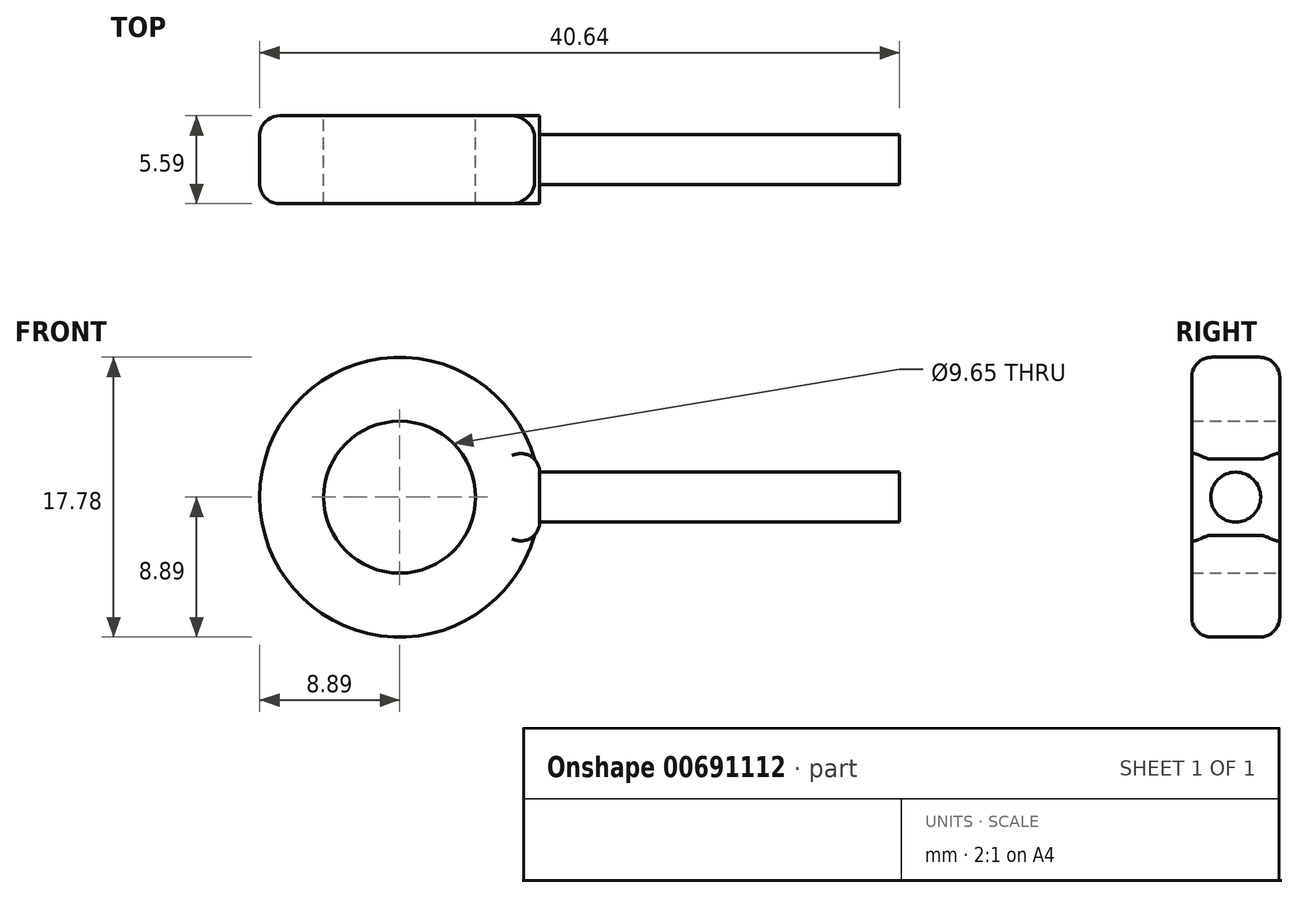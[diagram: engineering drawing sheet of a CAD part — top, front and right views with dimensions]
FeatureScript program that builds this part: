
annotation { "Feature Type Name" : "Feature", "Feature Type Description" : "" }
export const myFeature = defineFeature(function(context is Context, id is Id, definition is map)
    precondition{}
    {
        {
            var Q0;
            Q0=qCreatedBy(makeId("Front.planeOp"),FACE);
            var sketch = newSketch(context, id + "F0", { "sketchPlane" : qUnion([Q0])});
            skLineSegment(sketch, "E0", {"start": v(0, 0) * mm, "end": v(-95.2, 0) * mm, "construction": true});
            skLineSegment(sketch, "E1", {"start": v(0, 0) * mm, "end": v(0, 1.59) * mm});
            skLineSegment(sketch, "E2", {"start": v(0, 1.59) * mm, "end": v(-22.86, 1.59) * mm});
            skLineSegment(sketch, "E3.MirrorCS", {"start": v(0, -1.59) * mm, "end": v(-22.86, -1.59) * mm});
            skLineSegment(sketch, "E4.MirrorCS", {"start": v(0, 0) * mm, "end": v(0, -1.59) * mm});
            skLineSegment(sketch, "E5", {"start": v(-22.86, 1.59) * mm, "end": v(-22.86, -1.59) * mm});
            skArc(sketch, "E6", {"start": v(-23.2, 2.41) * mm, "mid": v(-40.64, 0) * mm, "end": v(-23.2, -2.41) * mm});
            skArc(sketch, "E7", {"start": v(-22.86, 1.59) * mm, "mid": v(-22.95, 2.03) * mm, "end": v(-23.2, 2.41) * mm});
            skArc(sketch, "E8", {"start": v(-22.86, -1.59) * mm, "mid": v(-22.95, -2.03) * mm, "end": v(-23.2, -2.41) * mm});
            skLineSegment(sketch, "E9", {"start": v(-23.2, 2.41) * mm, "end": v(-23.2, 0) * mm, "construction": true});
            skLineSegment(sketch, "E10", {"start": v(-23.2, 0) * mm, "end": v(-23.2, -2.41) * mm, "construction": true});
            skCircle(sketch, "E11", {"center": v(-31.75, 0) * mm, "radius": 4.83 * mm});
            skSolve(sketch);
        }
        {
            var Q0;
            Q0=makeQuery(id+"F0.imprint","IMPRINT",FACE,{"disambiguationData":[TD([[makeQuery(id+"F0.imprint","IMPRINT",EDGE,{"derivedFrom":sQuery(id+"F0.wireOp",EDGE,"E5")}),-1.0]])]});
            var Q1;
            Q1=makeQuery(id+"F0.imprint","IMPRINT",FACE,{"disambiguationData":[TD([[makeQuery(id+"F0.imprint","IMPRINT",EDGE,{"derivedFrom":sQuery(id+"F0.wireOp",EDGE,"E1")}),1.0]])]});
            extrude(context, id + "F1", {"entities" : qUnion([Q0, Q1]), "depth" : 5.6 * mm, "offsetDistance" : 25.4 * mm});
        }
        {
            var Q0;
            Q0=makeQuery(id+"F1.opExtrude","SWEPT_FACE",FACE,{"disambiguationData":[OSD([sQuery(id+"F0.wireOp",EDGE,"E1"),sQuery(id+"F0.wireOp",EDGE,"E4.MirrorCS")])]});
            var sketch = newSketch(context, id + "F2", { "sketchPlane" : qUnion([Q0])});
            skCircle(sketch, "E12", {"center": v(-2.8, 0) * mm, "radius": 1.59 * mm});
            skLineSegment(sketch, "E13", {"start": v(-5.59, -1.59) * mm, "end": v(-5.59, 1.59) * mm});
            skLineSegment(sketch, "E14", {"start": v(-5.59, 1.59) * mm, "end": v(0, 1.59) * mm});
            skLineSegment(sketch, "E15", {"start": v(0, 1.59) * mm, "end": v(0, -1.59) * mm});
            skLineSegment(sketch, "E16", {"start": v(0, -1.59) * mm, "end": v(-5.59, -1.59) * mm});
            skLineSegment(sketch, "E17", {"start": v(-5.59, 1.59) * mm, "end": v(0, -1.59) * mm, "construction": true});
            skSolve(sketch);
        }
        {
            var Q0;
            {var subQ0=sQuery(id+"F2.wireOp",EDGE,"E13");var subQ1=sQuery(id+"F2.wireOp",EDGE,"E12");var subQ2=makeQuery(id+"F2.imprint","INTERSECT",VERTEX,{"derivedFrom":[subQ1,subQ0]});Q0=makeQuery(id+"F2.imprint","IMPRINT",FACE,{"disambiguationData":[TD([[makeQuery(id+"F2.imprint","IMPRINT",EDGE,{"disambiguationData":[TD([[subQ2,-1.0]])],"derivedFrom":subQ1}),-1.0]])]});}
            var Q1;
            {var subQ0=sQuery(id+"F2.wireOp",EDGE,"E14");var subQ1=sQuery(id+"F2.wireOp",EDGE,"E12");var subQ2=makeQuery(id+"F2.imprint","INTERSECT",VERTEX,{"derivedFrom":[subQ1,subQ0]});Q1=makeQuery(id+"F2.imprint","IMPRINT",FACE,{"disambiguationData":[TD([[makeQuery(id+"F2.imprint","IMPRINT",EDGE,{"disambiguationData":[TD([[subQ2,-1.0]])],"derivedFrom":subQ1}),-1.0]])]});}
            var Q2;
            {var subQ0=sQuery(id+"F2.wireOp",EDGE,"E14");var subQ1=sQuery(id+"F2.wireOp",EDGE,"E12");var subQ2=makeQuery(id+"F2.imprint","INTERSECT",VERTEX,{"derivedFrom":[subQ1,subQ0]});Q2=makeQuery(id+"F2.imprint","IMPRINT",FACE,{"disambiguationData":[TD([[makeQuery(id+"F2.imprint","IMPRINT",EDGE,{"disambiguationData":[TD([[subQ2,1.0]])],"derivedFrom":subQ1}),-1.0]])]});}
            var Q3;
            {var subQ0=sQuery(id+"F2.wireOp",EDGE,"E15");var subQ1=sQuery(id+"F2.wireOp",EDGE,"E12");var subQ2=makeQuery(id+"F2.imprint","INTERSECT",VERTEX,{"derivedFrom":[subQ1,subQ0]});Q3=makeQuery(id+"F2.imprint","IMPRINT",FACE,{"disambiguationData":[TD([[makeQuery(id+"F2.imprint","IMPRINT",EDGE,{"disambiguationData":[TD([[subQ2,1.0]])],"derivedFrom":subQ1}),-1.0]])]});}
            var Q4;
            Q4=makeQuery(id+"F1.opExtrude","CAP_VERTEX",VERTEX,{"disambiguationData":[OSD([sQuery(id+"F0.wireOp",EDGE,"E3.MirrorCS"),sQuery(id+"F0.wireOp",EDGE,"E5"),sQuery(id+"F0.wireOp",EDGE,"E8")])],"isStart":false});
            extrude(context, id + "F3", {"entities" : qUnion([Q0, Q1, Q2, Q3]), "operationType" : NewBodyOperationType.REMOVE, "endBound" : BoundingType.UP_TO_VERTEX, "oppositeDirection" : true, "depth" : 25.4 * mm, "endBoundEntityVertex" : qUnion([Q4]), "offsetDistance" : 25.4 * mm});
        }
        {
            var Q0;
            Q0=makeQuery(id+"F1.opExtrude","CAP_EDGE",EDGE,{"disambiguationData":[OSD([sQuery(id+"F0.wireOp",EDGE,"E6")])],"isStart":true});
            fillet(context, id + "F4", {"entities" : qUnion([Q0]), "radius" : 1.27 * mm, "allowEdgeOverflow" : false});
        }
        {
            var Q0;
            Q0=makeQuery(id+"F1.opExtrude","CAP_EDGE",EDGE,{"disambiguationData":[OSD([sQuery(id+"F0.wireOp",EDGE,"E6")])],"isStart":false});
            fillet(context, id + "F5", {"entities" : qUnion([Q0]), "radius" : 1.27 * mm, "tangentPropagation" : true, "allowEdgeOverflow" : false});
        }
    });
